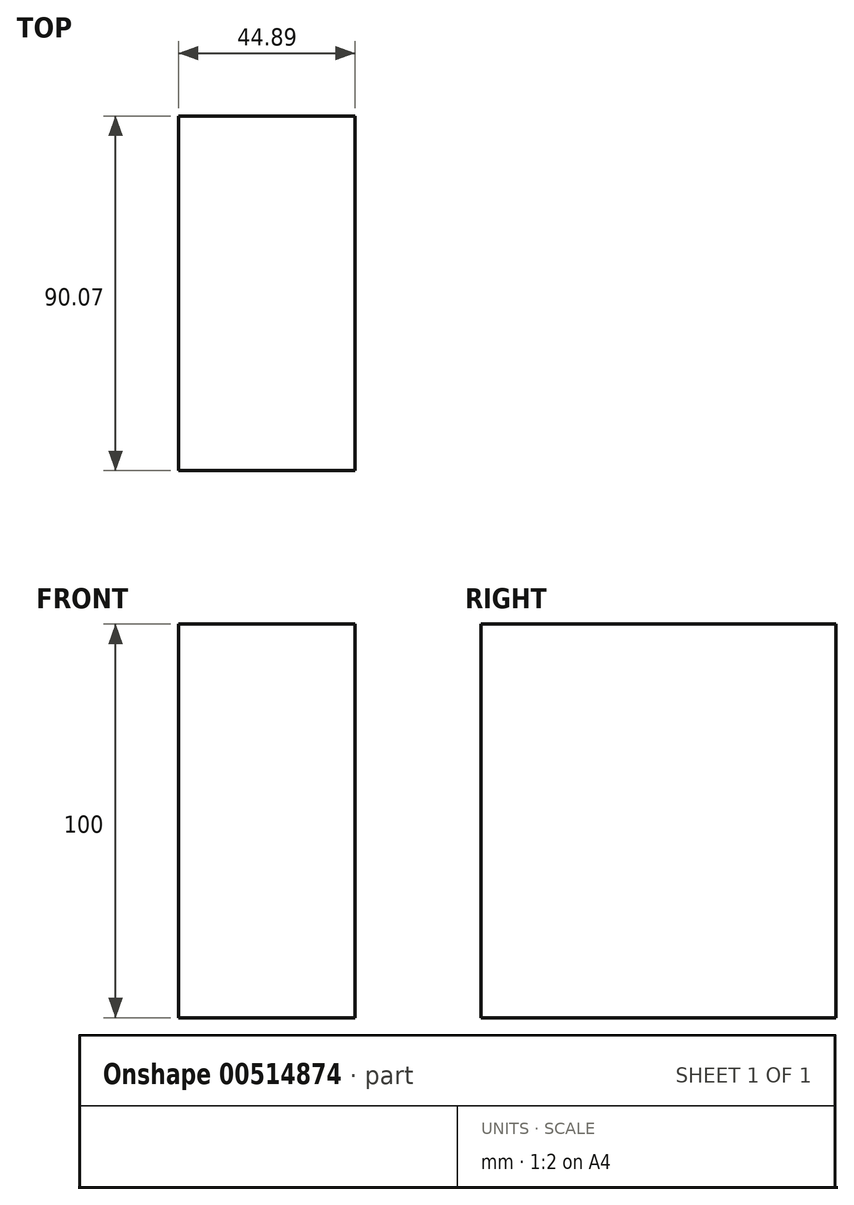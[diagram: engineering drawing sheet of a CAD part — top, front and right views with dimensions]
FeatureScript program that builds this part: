
annotation { "Feature Type Name" : "Feature", "Feature Type Description" : "" }
export const myFeature = defineFeature(function(context is Context, id is Id, definition is map)
    precondition{}
    {
        {
            var Q0;
            Q0=qCreatedBy(makeId("Top.planeOp"),FACE);
            var sketch = newSketch(context, id + "F0", { "sketchPlane" : qUnion([Q0])});
            skLineSegment(sketch, "E0.bottom", {"start": v(7.58, -14.14) * mm, "end": v(-37.3, -14.14) * mm});
            skLineSegment(sketch, "E0.top", {"start": v(7.58, 75.93) * mm, "end": v(-37.3, 75.93) * mm});
            skLineSegment(sketch, "E0.left", {"start": v(7.58, -14.14) * mm, "end": v(7.58, 75.93) * mm});
            skLineSegment(sketch, "E0.right", {"start": v(-37.3, -14.14) * mm, "end": v(-37.3, 75.93) * mm});
            skSolve(sketch);
        }
        {
            var Q0;
            Q0=makeQuery(id+"F0.imprint","IMPRINT",FACE,{"disambiguationData":[TD([[makeQuery(id+"F0.imprint","IMPRINT",EDGE,{"derivedFrom":sQuery(id+"F0.wireOp",EDGE,"E0.bottom")}),-1.0]])]});
            extrude(context, id + "F1", {"entities" : qUnion([Q0]), "depth" : 100 * mm, "offsetDistance" : 25.4 * mm});
        }
    });
